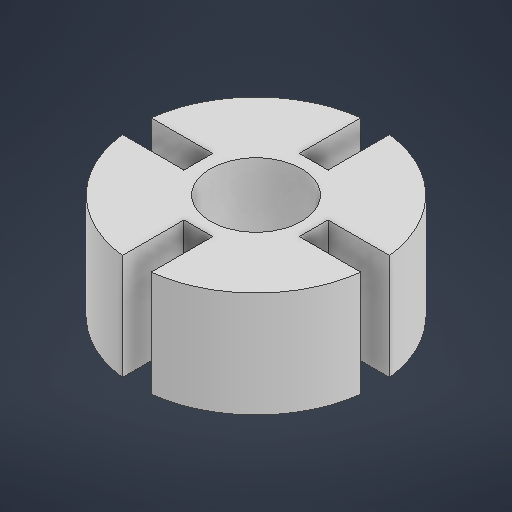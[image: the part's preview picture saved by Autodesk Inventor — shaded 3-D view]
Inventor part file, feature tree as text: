
AUTODESK INVENTOR PART (.ipt)
format: ipt  version: 2025.3 (Build 293356000, 356)  size: 196,608 bytes
history: native  units: mm
features: sketch x2, extrude x1
ambient origin geometry x8: Origin, YZ Plane, XZ Plane, XY Plane, X Axis, Y Axis, Z Axis, Center Point
bodies: Solid1 (feature_tree)
feature tree (3):
  extrude  "Extrusion1"  Depth=6.0mm
  sketch  "Sketch1"  dims[d0=50.0mm d1=6.0mm]
  sketch  "Sketch Circular Pattern1"  dims[d3=19.0mm d4=12.0mm d5=15.0mm d6=40.0mm d8=360.0deg d10=22.0mm d11=0.0mm]
